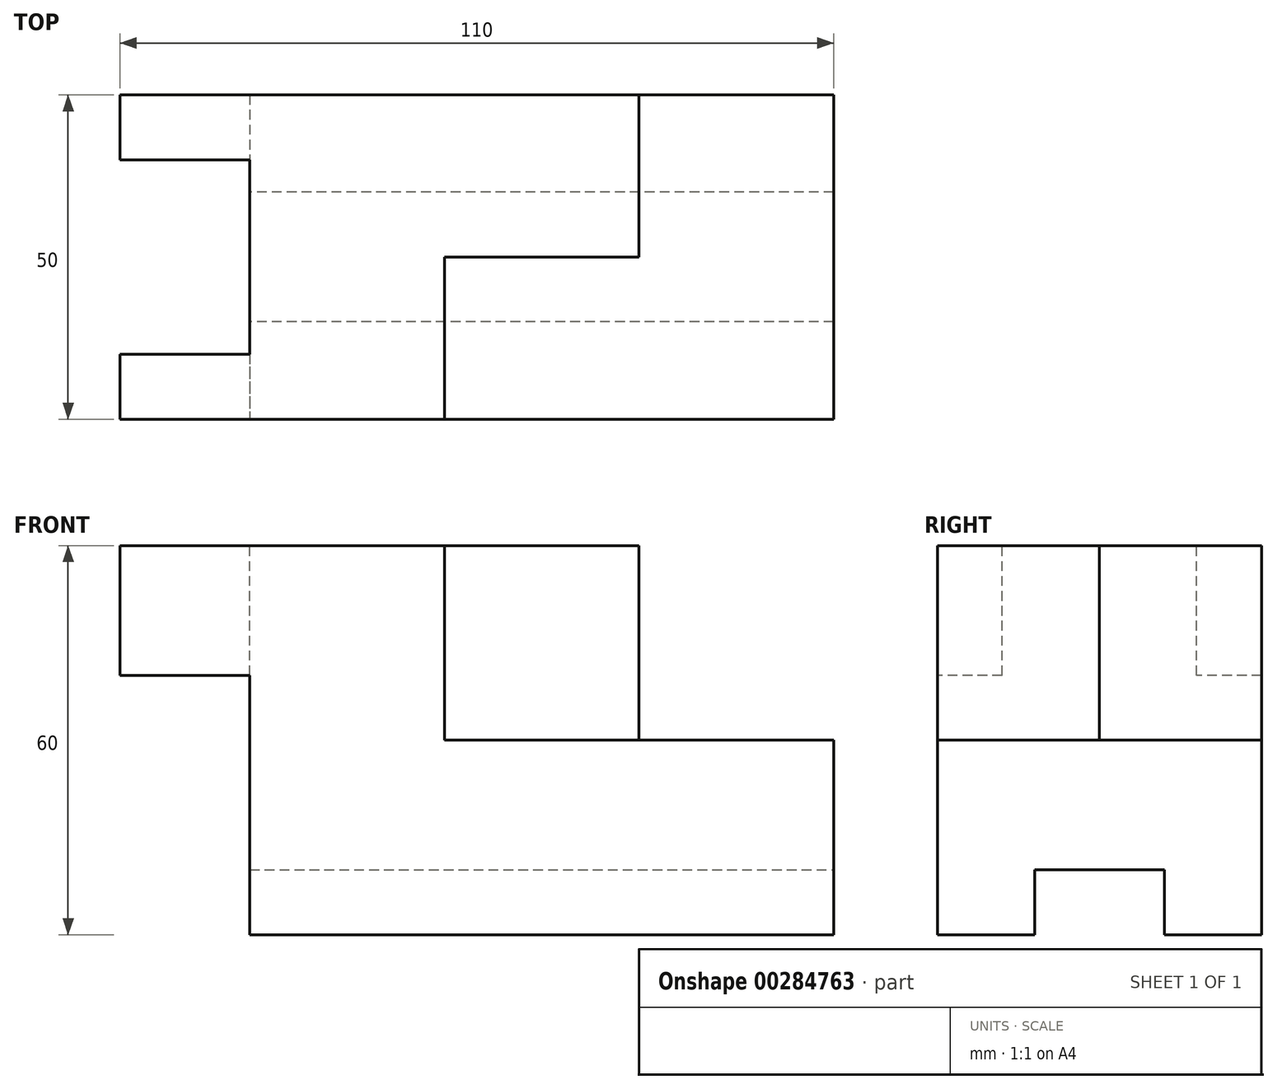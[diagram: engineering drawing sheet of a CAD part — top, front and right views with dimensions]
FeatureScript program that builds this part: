
annotation { "Feature Type Name" : "Feature", "Feature Type Description" : "" }
export const myFeature = defineFeature(function(context is Context, id is Id, definition is map)
    precondition{}
    {
        {
            var Q0;
            Q0=qCreatedBy(makeId("Top.planeOp"),FACE);
            var sketch = newSketch(context, id + "F0", { "sketchPlane" : qUnion([Q0])});
            skLineSegment(sketch, "E0.bottom", {"start": v(-55, 25) * mm, "end": v(55, 25) * mm});
            skLineSegment(sketch, "E0.top", {"start": v(-55, -25) * mm, "end": v(55, -25) * mm});
            skLineSegment(sketch, "E0.left", {"start": v(-55, 25) * mm, "end": v(-55, -25) * mm});
            skLineSegment(sketch, "E0.right", {"start": v(55, 25) * mm, "end": v(55, -25) * mm});
            skPoint(sketch, "E0.middle", {"position": v(0, 0) * mm});
            skSolve(sketch);
        }
        {
            var Q0;
            Q0 = qSketchRegion(id + "F0", true);
            extrude(context, id + "F1", {"entities" : qUnion([Q0]), "depth" : 60 * mm});
        }
        {
            var Q0;
            Q0=makeQuery(id+"F1.opExtrude","CAP_FACE",FACE,{"disambiguationData":[OSD([sQuery(id+"F0.wireOp",EDGE,"E0.bottom"),sQuery(id+"F0.wireOp",EDGE,"E0.top"),sQuery(id+"F0.wireOp",EDGE,"E0.left"),sQuery(id+"F0.wireOp",EDGE,"E0.right")])],"isStart":false});
            var sketch = newSketch(context, id + "F2", { "sketchPlane" : qUnion([Q0])});
            skLineSegment(sketch, "E1", {"start": v(25, 25) * mm, "end": v(25, 0) * mm});
            skLineSegment(sketch, "E2", {"start": v(25, 0) * mm, "end": v(-5, 0) * mm});
            skLineSegment(sketch, "E3", {"start": v(-5, 0) * mm, "end": v(-5, -25) * mm});
            skLineSegment(sketch, "E4", {"start": v(-5, -25) * mm, "end": v(55, -25) * mm});
            skLineSegment(sketch, "E5", {"start": v(55, -25) * mm, "end": v(55, 25) * mm});
            skLineSegment(sketch, "E6", {"start": v(55, 25) * mm, "end": v(25, 25) * mm});
            skSolve(sketch);
        }
        {
            var Q0;
            Q0 = qSketchRegion(id + "F2", true);
            extrude(context, id + "F3", {"entities" : qUnion([Q0]), "operationType" : NewBodyOperationType.REMOVE, "oppositeDirection" : true, "depth" : 30 * mm});
        }
        {
            var Q0;
            Q0=makeQuery(id+"F1.opExtrude","SWEPT_FACE",FACE,{"disambiguationData":[OSD([sQuery(id+"F0.wireOp",EDGE,"E0.right")])]});
            var sketch = newSketch(context, id + "F4", { "sketchPlane" : qUnion([Q0])});
            skLineSegment(sketch, "E7.bottom", {"start": v(10, -10) * mm, "end": v(-10, -10) * mm});
            skLineSegment(sketch, "E7.top", {"start": v(10, 10) * mm, "end": v(-10, 10) * mm});
            skLineSegment(sketch, "E7.left", {"start": v(10, -10) * mm, "end": v(10, 10) * mm});
            skLineSegment(sketch, "E7.right", {"start": v(-10, -10) * mm, "end": v(-10, 10) * mm});
            skPoint(sketch, "E7.middle", {"position": v(0, 0) * mm});
            skSolve(sketch);
        }
        {
            var Q0;
            Q0 = qSketchRegion(id + "F4", true);
            extrude(context, id + "F5", {"entities" : qUnion([Q0]), "operationType" : NewBodyOperationType.REMOVE, "endBound" : BoundingType.THROUGH_ALL, "oppositeDirection" : true, "depth" : 25 * mm});
        }
        {
            var Q0;
            Q0=makeQuery(id+"F1.opExtrude","CAP_FACE",FACE,{"disambiguationData":[OSD([sQuery(id+"F0.wireOp",EDGE,"E0.bottom"),sQuery(id+"F0.wireOp",EDGE,"E0.top"),sQuery(id+"F0.wireOp",EDGE,"E0.left"),sQuery(id+"F0.wireOp",EDGE,"E0.right")])],"isStart":false});
            var sketch = newSketch(context, id + "F6", { "sketchPlane" : qUnion([Q0])});
            skLineSegment(sketch, "E8.bottom", {"start": v(-35, 15) * mm, "end": v(-75, 15) * mm});
            skLineSegment(sketch, "E8.top", {"start": v(-35, -15) * mm, "end": v(-75, -15) * mm});
            skLineSegment(sketch, "E8.left", {"start": v(-35, 15) * mm, "end": v(-35, -15) * mm});
            skLineSegment(sketch, "E8.right", {"start": v(-75, 15) * mm, "end": v(-75, -15) * mm});
            skPoint(sketch, "E8.middle", {"position": v(-55, 0) * mm});
            skSolve(sketch);
        }
        {
            var Q0;
            Q0 = qSketchRegion(id + "F6", true);
            extrude(context, id + "F7", {"entities" : qUnion([Q0]), "operationType" : NewBodyOperationType.REMOVE, "endBound" : BoundingType.THROUGH_ALL, "oppositeDirection" : true, "depth" : 25 * mm});
        }
        {
            var Q0;
            Q0=makeQuery(id+"F1.opExtrude","SWEPT_FACE",FACE,{"disambiguationData":[OSD([sQuery(id+"F0.wireOp",EDGE,"E0.top")])]});
            var sketch = newSketch(context, id + "F8", { "sketchPlane" : qUnion([Q0])});
            skLineSegment(sketch, "E9.bottom", {"start": v(-55, 0) * mm, "end": v(-35, 0) * mm});
            skLineSegment(sketch, "E9.top", {"start": v(-55, 40) * mm, "end": v(-35, 40) * mm});
            skLineSegment(sketch, "E9.left", {"start": v(-55, 0) * mm, "end": v(-55, 40) * mm});
            skLineSegment(sketch, "E9.right", {"start": v(-35, 0) * mm, "end": v(-35, 40) * mm});
            skSolve(sketch);
        }
        {
            var Q0;
            Q0 = qSketchRegion(id + "F8", true);
            extrude(context, id + "F9", {"entities" : qUnion([Q0]), "operationType" : NewBodyOperationType.REMOVE, "endBound" : BoundingType.THROUGH_ALL, "oppositeDirection" : true, "depth" : 25 * mm});
        }
    });
